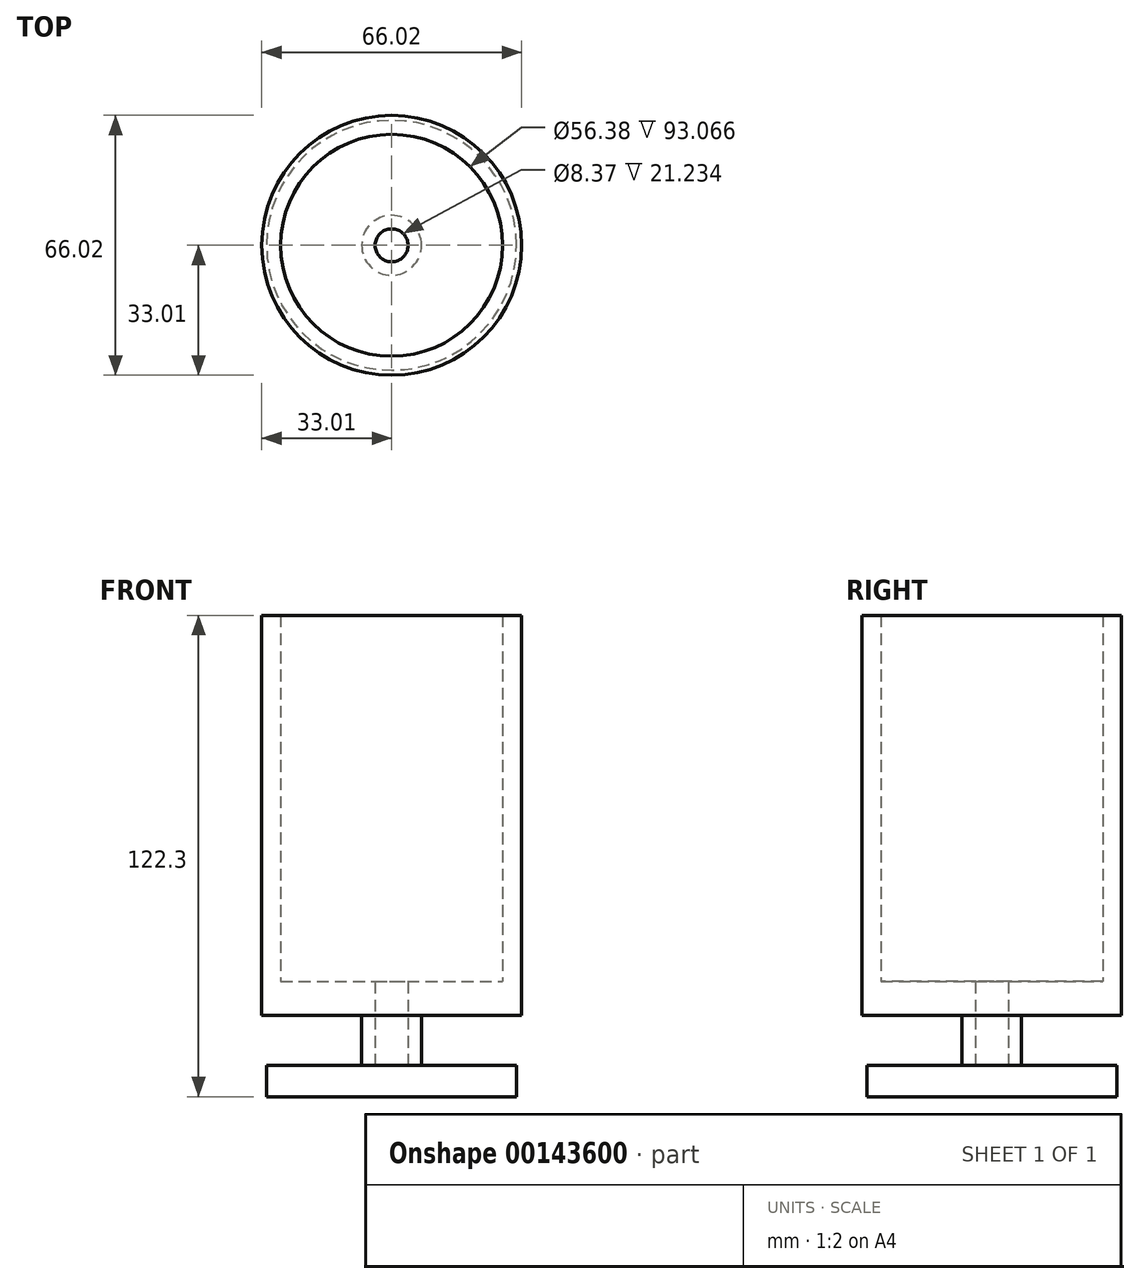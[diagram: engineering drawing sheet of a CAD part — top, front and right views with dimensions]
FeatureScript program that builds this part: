
annotation { "Feature Type Name" : "Feature", "Feature Type Description" : "" }
export const myFeature = defineFeature(function(context is Context, id is Id, definition is map)
    precondition{}
    {
        {
            var Q0;
            Q0=qCreatedBy(makeId("Front.planeOp"),FACE);
            var sketch = newSketch(context, id + "F0", { "sketchPlane" : qUnion([Q0])});
            skLineSegment(sketch, "E0", {"start": v(0, 0) * mm, "end": v(31.75, 0) * mm});
            skLineSegment(sketch, "E1", {"start": v(31.75, 0) * mm, "end": v(31.75, 8) * mm});
            skLineSegment(sketch, "E2", {"start": v(31.75, 8) * mm, "end": v(0, 8) * mm});
            skLineSegment(sketch, "E3", {"start": v(7.6, 8) * mm, "end": v(7.6, 20.7) * mm});
            skLineSegment(sketch, "E4", {"start": v(7.6, 20.7) * mm, "end": v(33, 20.7) * mm});
            skLineSegment(sketch, "E5", {"start": v(33, 20.7) * mm, "end": v(33, 122.3) * mm});
            skLineSegment(sketch, "E6", {"start": v(33, 122.3) * mm, "end": v(28.19, 122.3) * mm});
            skLineSegment(sketch, "E7", {"start": v(28.19, 122.3) * mm, "end": v(28.19, 29.23) * mm});
            skLineSegment(sketch, "E8", {"start": v(28.19, 29.23) * mm, "end": v(4.19, 29.23) * mm});
            skLineSegment(sketch, "E9", {"start": v(4.19, 29.23) * mm, "end": v(4.19, 8) * mm});
            skLineSegment(sketch, "E10", {"start": v(0, 0) * mm, "end": v(0, 8) * mm});
            skSolve(sketch);
        }
        {
            var Q0;
            Q0=makeQuery(id+"F0.imprint","IMPRINT",FACE,{"disambiguationData":[TD([[makeQuery(id+"F0.imprint","IMPRINT",EDGE,{"derivedFrom":sQuery(id+"F0.wireOp",EDGE,"E0")}),1.0]])]});
            var Q1;
            {var subQ0=sQuery(id+"F0.wireOp",EDGE,"E3");Q1=makeQuery(id+"F0.imprint","IMPRINT",FACE,{"disambiguationData":[TD([[makeQuery(id+"F0.imprint","IMPRINT",EDGE,{"derivedFrom":subQ0}),1.0]])]});}
            var Q2;
            Q2=sQuery(id+"F0.wireOp",EDGE,"E10");
            revolve(context, id + "F1", {"entities" : qUnion([Q0, Q1]), "axis" : qUnion([Q2]), "revolveType" : RevolveType.FULL});
        }
    });
